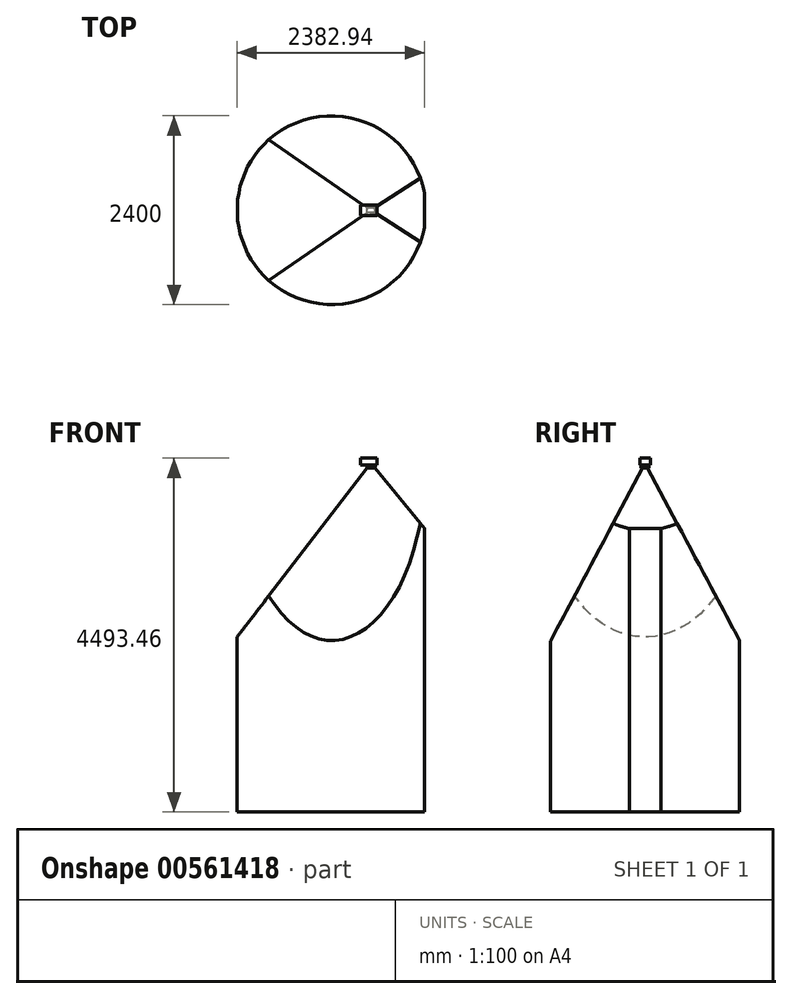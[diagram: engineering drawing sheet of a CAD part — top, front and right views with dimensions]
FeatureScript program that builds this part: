
annotation { "Feature Type Name" : "Feature", "Feature Type Description" : "" }
export const myFeature = defineFeature(function(context is Context, id is Id, definition is map)
    precondition{}
    {
        {
            var Q0;
            Q0=qCreatedBy(makeId("Top.planeOp"),FACE);
            var sketch = newSketch(context, id + "F0", { "sketchPlane" : qUnion([Q0])});
            skLineSegment(sketch, "E0.bottom", {"start": v(-130, 67.5) * mm, "end": v(80, 67.5) * mm});
            skLineSegment(sketch, "E0.top", {"start": v(-130, -67.5) * mm, "end": v(80, -67.5) * mm});
            skLineSegment(sketch, "E0.left", {"start": v(-130, 67.5) * mm, "end": v(-130, -67.5) * mm});
            skLineSegment(sketch, "E0.right", {"start": v(80, 67.5) * mm, "end": v(80, -67.5) * mm});
            skSolve(sketch);
        }
        {
            var Q0;
            Q0=makeQuery(id+"F0.imprint","IMPRINT",FACE,{"disambiguationData":[TD([[makeQuery(id+"F0.imprint","IMPRINT",EDGE,{"derivedFrom":sQuery(id+"F0.wireOp",EDGE,"E0.bottom")}),-1.0]])]});
            extrude(context, id + "F1", {"entities" : qUnion([Q0]), "depth" : 125 * mm, "offsetDistance" : 25.4 * mm});
        }
        {
            var Q0;
            Q0=makeQuery(id+"F1.opExtrude","CAP_FACE",FACE,{"disambiguationData":[OSD([sQuery(id+"F0.wireOp",EDGE,"E0.bottom"),sQuery(id+"F0.wireOp",EDGE,"E0.top"),sQuery(id+"F0.wireOp",EDGE,"E0.left"),sQuery(id+"F0.wireOp",EDGE,"E0.right")])],"isStart":true});
            var sketch = newSketch(context, id + "F2", { "sketchPlane" : qUnion([Q0])});
            skCircle(sketch, "E1", {"center": v(0.4, 0) * mm, "radius": 50.8 * mm});
            skLineSegment(sketch, "E2.0", {"start": v(-130, -67.5) * mm, "end": v(-130, 67.5) * mm});
            skLineSegment(sketch, "E3.0", {"start": v(-130, 67.5) * mm, "end": v(80, 67.5) * mm});
            skLineSegment(sketch, "E4.0", {"start": v(80, -67.5) * mm, "end": v(80, 67.5) * mm});
            skLineSegment(sketch, "E5.0", {"start": v(-130, -67.5) * mm, "end": v(80, -67.5) * mm});
            skLineSegment(sketch, "E6", {"start": v(-25, -67.5) * mm, "end": v(-25, 67.5) * mm, "construction": true});
            skPoint(sketch, "E7.endSnap0", {"position": v(-130, 0) * mm});
            skLineSegment(sketch, "E8.trimOffspring", {"start": v(-130, 0) * mm, "end": v(-499.6, 0) * mm, "construction": true});
            skCircle(sketch, "E9", {"center": v(-499.6, 0) * mm, "radius": 1200 * mm});
            skLineSegment(sketch, "E10", {"start": v(0, 0) * mm, "end": v(0, 1091.05) * mm});
            skLineSegment(sketch, "E11", {"start": v(0.4, 0) * mm, "end": v(0.4, -1090.87) * mm});
            skSolve(sketch);
        }
        {
            var Q0;
            Q0=makeQuery(id+"F2.imprint","IMPRINT",FACE,{"disambiguationData":[TD([[makeQuery(id+"F2.imprint","IMPRINT",EDGE,{"derivedFrom":sQuery(id+"F2.wireOp",EDGE,"E1")}),-1.0]])]});
            extrude(context, id + "F3", {"entities" : qUnion([Q0]), "operationType" : NewBodyOperationType.REMOVE, "oppositeDirection" : true, "depth" : 40 * mm, "offsetDistance" : 25.4 * mm});
        }
        {
            var Q0;
            Q0=makeQuery(id+"F1.opExtrude","SWEPT_FACE",FACE,{"disambiguationData":[OSD([sQuery(id+"F0.wireOp",EDGE,"E0.top")])]});
            var sketch = newSketch(context, id + "F4", { "sketchPlane" : qUnion([Q0])});
            skLineSegment(sketch, "E12", {"start": v(-25, 125) * mm, "end": v(-25, 82.5) * mm, "construction": true});
            skPoint(sketch, "E12.endSnap0", {"position": v(-130, 82.5) * mm});
            skCircle(sketch, "E13", {"center": v(-25, 82.5) * mm, "radius": 5 * mm});
            skSolve(sketch);
        }
        {
            var Q0;
            Q0=qCreatedBy(makeId("Front.planeOp"),FACE);
            var sketch = newSketch(context, id + "F5", { "sketchPlane" : qUnion([Q0])});
            skLineSegment(sketch, "E14.0", {"start": v(51.2, 0) * mm, "end": v(-50.4, 0) * mm});
            skLineSegment(sketch, "E15.0", {"start": v(-130, 125) * mm, "end": v(80, 125) * mm});
            skLineSegment(sketch, "E16.0", {"start": v(-130, 40) * mm, "end": v(80, 40) * mm});
            skLineSegment(sketch, "E17", {"start": v(0, 0) * mm, "end": v(0, 61.5) * mm});
            skLineSegment(sketch, "E18", {"start": v(0, 61.5) * mm, "end": v(683.34, -769.64) * mm});
            skLineSegment(sketch, "E19", {"start": v(683.34, -4368.46) * mm, "end": v(0, -4368.46) * mm});
            skLineSegment(sketch, "E20", {"start": v(0, -4368.46) * mm, "end": v(-686.08, -4368.46) * mm});
            skLineSegment(sketch, "E21", {"start": v(-1699.6, -2147.57) * mm, "end": v(0, 61.5) * mm});
            skLineSegment(sketch, "E22.right", {"start": v(0, -4368.46) * mm, "end": v(0, 61.5) * mm});
            skLineSegment(sketch, "E23.bottom", {"start": v(683.34, -4368.46) * mm, "end": v(0, -4429.62) * mm});
            skLineSegment(sketch, "E23.right", {"start": v(0, -4429.62) * mm, "end": v(0, 61.5) * mm});
            skLineSegment(sketch, "E24", {"start": v(-686.08, -4368.46) * mm, "end": v(-686.08, -830.23) * mm, "construction": true});
            skLineSegment(sketch, "E25", {"start": v(683.34, -4368.46) * mm, "end": v(683.34, -769.64) * mm});
            skLineSegment(sketch, "E26", {"start": v(-686.08, -4368.46) * mm, "end": v(-1699.6, -4368.46) * mm});
            skLineSegment(sketch, "E27.0", {"start": v(700.4, 0) * mm, "end": v(-1699.6, 0) * mm});
            skLineSegment(sketch, "E28", {"start": v(-1699.6, -2147.57) * mm, "end": v(-1699.6, -4368.46) * mm});
            skSolve(sketch);
        }
        {
            var Q0;
            Q0=qCreatedBy(makeId("Right.planeOp"),FACE);
            var sketch = newSketch(context, id + "F6", { "sketchPlane" : qUnion([Q0])});
            skLineSegment(sketch, "E29", {"start": v(0, 61.5) * mm, "end": v(-1200, -2195.37) * mm});
            skLineSegment(sketch, "E30", {"start": v(1200, -2195.37) * mm, "end": v(0, 61.5) * mm});
            skLineSegment(sketch, "E31", {"start": v(-1200, -2195.37) * mm, "end": v(0, -2195.37) * mm});
            skLineSegment(sketch, "E32", {"start": v(0, 61.5) * mm, "end": v(0, -2195.37) * mm});
            skLineSegment(sketch, "E33", {"start": v(0, -2195.37) * mm, "end": v(1200, -2195.37) * mm});
            skLineSegment(sketch, "E34", {"start": v(-1200, -2195.37) * mm, "end": v(-1200, -4438.5) * mm});
            skLineSegment(sketch, "E35", {"start": v(1200, -2195.37) * mm, "end": v(1200, -4438.5) * mm});
            skLineSegment(sketch, "E36", {"start": v(-1200, -4438.5) * mm, "end": v(1200, -4438.5) * mm});
            skLineSegment(sketch, "E37.right", {"start": v(0, 10.7) * mm, "end": v(0, 61.5) * mm});
            skLineSegment(sketch, "E38.left", {"start": v(0, 61.5) * mm, "end": v(0, 10.7) * mm});
            skSolve(sketch);
        }
        {
            var Q0;
            Q0=sQuery(id+"F5.wireOp",VERTEX,"E20.start");
            var Q1;
            Q1=sQuery(id+"F5.wireOp",EDGE,"E23.right");
            cPlane(context, id + "F7", {"entities" : qUnion([Q0, Q1]), "cplaneType" : CPlaneType.LINE_POINT, "offset" : 25.4 * mm, "width" : 152.4 * mm, "height" : 152.4 * mm});
        }
        {
            var Q0;
            Q0=sQuery(id+"F2.wireOp",EDGE,"E9");
            var Q1;
            Q1=sQuery(id+"F5.wireOp",VERTEX,"E20.start");
            extrude(context, id + "F8", {"bodyType" : ToolBodyType.SURFACE, "surfaceEntities" : qUnion([Q0]), "endBound" : BoundingType.UP_TO_VERTEX, "depth" : 25.4 * mm, "endBoundEntityVertex" : qUnion([Q1]), "offsetDistance" : 25.4 * mm});
        }
        {
            var Q0;
            Q0=makeQuery(id+"F5.imprint","IMPRINT",FACE,{"disambiguationData":[TD([[makeQuery(id+"F5.imprint","IMPRINT",EDGE,{"derivedFrom":sQuery(id+"F5.wireOp",EDGE,"E20")}),-1.0]])]});
            var Q1;
            {var subQ1=sQuery(id+"F5.wireOp",EDGE,"E19");Q1=makeQuery(id+"F5.imprint","IMPRINT",FACE,{"disambiguationData":[TD([[makeQuery(id+"F5.imprint","IMPRINT",EDGE,{"derivedFrom":subQ1}),-1.0]])]});}
            var Q2;
            Q2=makeQuery(id+"F8.opExtrude","SWEPT_FACE",FACE,{"disambiguationData":[OSD([sQuery(id+"F2.wireOp",EDGE,"E9")])]});
            var Q3;
            Q3=makeQuery(id+"F8.opExtrude","SWEPT_FACE",FACE,{"disambiguationData":[OSD([sQuery(id+"F2.wireOp",EDGE,"E9")])]});
            extrude(context, id + "F9", {"entities" : qUnion([Q0, Q1]), "endBound" : BoundingType.UP_TO_SURFACE, "depth" : 25.4 * mm, "endBoundEntityFace" : qUnion([Q2]), "offsetDistance" : 25.4 * mm, "hasSecondDirection" : true, "secondDirectionBound" : SecondDirectionBoundingType.UP_TO_SURFACE, "secondDirectionOppositeDirection" : true, "secondDirectionDepth" : 25.4 * mm, "secondDirectionBoundEntityFace" : qUnion([Q3])});
        }
        {
            var Q0;
            Q0=makeQuery(id+"F6.imprint","IMPRINT",FACE,{"disambiguationData":[TD([[makeQuery(id+"F6.imprint","IMPRINT",EDGE,{"derivedFrom":sQuery(id+"F6.wireOp",EDGE,"E30")}),1.0]])]});
            var Q1;
            Q1=makeQuery(id+"F6.imprint","IMPRINT",FACE,{"disambiguationData":[TD([[makeQuery(id+"F6.imprint","IMPRINT",EDGE,{"derivedFrom":sQuery(id+"F6.wireOp",EDGE,"E31")}),-1.0]])]});
            var Q2;
            Q2=makeQuery(id+"F6.imprint","IMPRINT",FACE,{"disambiguationData":[TD([[makeQuery(id+"F6.imprint","IMPRINT",EDGE,{"derivedFrom":sQuery(id+"F6.wireOp",EDGE,"E29")}),1.0]])]});
            var Q3;
            Q3=makeQuery(id+"F8.opExtrude","SWEPT_FACE",FACE,{"disambiguationData":[OSD([sQuery(id+"F2.wireOp",EDGE,"E9")])]});
            var Q4;
            Q4=makeQuery(id+"F8.opExtrude","SWEPT_FACE",FACE,{"disambiguationData":[OSD([sQuery(id+"F2.wireOp",EDGE,"E9")])]});
            extrude(context, id + "F10", {"entities" : qUnion([Q0, Q1, Q2]), "endBound" : BoundingType.UP_TO_SURFACE, "oppositeDirection" : true, "depth" : 25.4 * mm, "endBoundEntityFace" : qUnion([Q3]), "offsetDistance" : 25.4 * mm, "hasSecondDirection" : true, "secondDirectionBound" : SecondDirectionBoundingType.UP_TO_SURFACE, "secondDirectionOppositeDirection" : false, "secondDirectionDepth" : 25.4 * mm, "secondDirectionBoundEntityFace" : qUnion([Q4])});
        }
        {
            var Q0;
            Q0=makeQuery(id+"F9.opExtrude","SWEPT_BODY",BODY,{"disambiguationData":[OSD([sQuery(id+"F5.wireOp",EDGE,"E18"),sQuery(id+"F5.wireOp",EDGE,"E21"),sQuery(id+"F5.wireOp",EDGE,"E22.bottom"),sQuery(id+"F5.wireOp",EDGE,"E23.bottom"),sQuery(id+"F5.wireOp",EDGE,"NObzXFAz-WtYv-HaUj-2brL-z7mSbjSfYPqi"),sQuery(id+"F5.wireOp",EDGE,"GQ5a5nGe-0pfp-PTgc-u2Mi-eE7iz8itg5FN")])]});
            var Q1;
            Q1=makeQuery(id+"F10.opExtrude","SWEPT_BODY",BODY,{"disambiguationData":[OSD([sQuery(id+"F6.wireOp",EDGE,"E29"),sQuery(id+"F6.wireOp",EDGE,"E30"),sQuery(id+"F6.wireOp",EDGE,"E34"),sQuery(id+"F6.wireOp",EDGE,"E35"),sQuery(id+"F6.wireOp",EDGE,"E36")])]});
            booleanBodies(context, id + "F11", {"operationType" : BooleanOperationType.INTERSECTION, "tools" : qUnion([Q0, Q1])});
        }
    });
